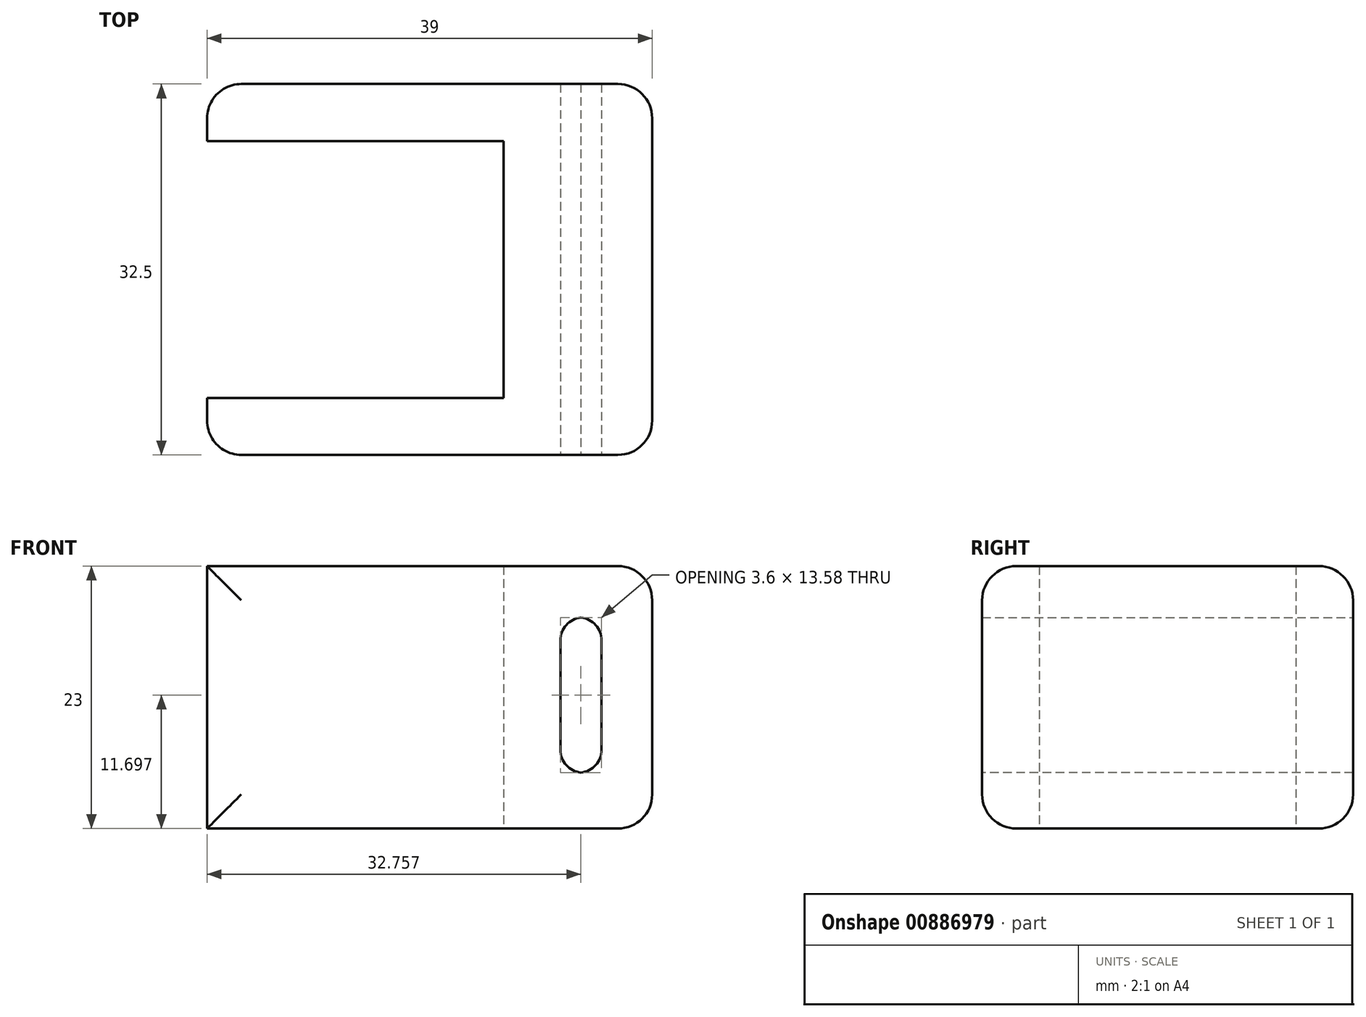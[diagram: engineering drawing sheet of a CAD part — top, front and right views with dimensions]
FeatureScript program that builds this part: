
annotation { "Feature Type Name" : "Feature", "Feature Type Description" : "" }
export const myFeature = defineFeature(function(context is Context, id is Id, definition is map)
    precondition{}
    {
        {
            var Q0;
            Q0=qCreatedBy(makeId("Top.planeOp"),FACE);
            var sketch = newSketch(context, id + "F0", { "sketchPlane" : qUnion([Q0])});
            skLineSegment(sketch, "E0", {"start": v(12.77, 15.26) * mm, "end": v(12.77, -17.24) * mm});
            skLineSegment(sketch, "E1", {"start": v(12.77, -17.24) * mm, "end": v(-26.23, -17.24) * mm});
            skLineSegment(sketch, "E2", {"start": v(-26.23, -17.24) * mm, "end": v(-26.23, -12.24) * mm});
            skLineSegment(sketch, "E3", {"start": v(-26.23, -12.24) * mm, "end": v(-0.23, -12.24) * mm});
            skLineSegment(sketch, "E4", {"start": v(-0.23, -12.24) * mm, "end": v(-0.23, 10.26) * mm});
            skLineSegment(sketch, "E5", {"start": v(-0.23, 10.26) * mm, "end": v(-26.23, 10.26) * mm});
            skLineSegment(sketch, "E6", {"start": v(-26.23, 10.26) * mm, "end": v(-26.23, 15.26) * mm});
            skLineSegment(sketch, "E7", {"start": v(-26.23, 15.26) * mm, "end": v(12.77, 15.26) * mm});
            skSolve(sketch);
        }
        {
            var Q0;
            Q0=makeQuery(id+"F0.imprint","IMPRINT",FACE,{"disambiguationData":[TD([[makeQuery(id+"F0.imprint","IMPRINT",EDGE,{"derivedFrom":sQuery(id+"F0.wireOp",EDGE,"E0")}),-1.0]])]});
            extrude(context, id + "F1", {"entities" : qUnion([Q0]), "depth" : 23 * mm, "offsetDistance" : 25 * mm});
        }
        {
            var Q0;
            Q0=makeQuery(id+"F1.opExtrude","SWEPT_FACE",FACE,{"disambiguationData":[OSD([sQuery(id+"F0.wireOp",EDGE,"E1")])]});
            var sketch = newSketch(context, id + "F2", { "sketchPlane" : qUnion([Q0])});
            skLineSegment(sketch, "E8.bottom", {"start": v(8.33, 18.5) * mm, "end": v(4.73, 18.5) * mm});
            skLineSegment(sketch, "E8.top", {"start": v(8.33, 4.9) * mm, "end": v(4.73, 4.9) * mm});
            skLineSegment(sketch, "E8.left", {"start": v(8.33, 18.5) * mm, "end": v(8.33, 4.9) * mm});
            skLineSegment(sketch, "E8.right", {"start": v(4.73, 18.5) * mm, "end": v(4.73, 4.9) * mm});
            skSolve(sketch);
        }
        {
            var Q0;
            Q0=makeQuery(id+"F2.imprint","IMPRINT",FACE,{"disambiguationData":[TD([[makeQuery(id+"F2.imprint","IMPRINT",EDGE,{"derivedFrom":sQuery(id+"F2.wireOp",EDGE,"E8.bottom")}),1.0]])]});
            extrude(context, id + "F3", {"entities" : qUnion([Q0]), "operationType" : NewBodyOperationType.REMOVE, "oppositeDirection" : true, "depth" : 48.7 * mm, "offsetDistance" : 25 * mm});
        }
        {
            var Q0;
            Q0=makeQuery(id+"F3.boolean.opBoolean","COPY",EDGE,{"derivedFrom":makeQuery(id+"F3.opExtrude","SWEPT_EDGE",EDGE,{"disambiguationData":[OSD([sQuery(id+"F2.wireOp",EDGE,"E8.bottom"),sQuery(id+"F2.wireOp",EDGE,"E8.right")])]})});
            var Q1;
            Q1=makeQuery(id+"F3.boolean.opBoolean","COPY",EDGE,{"derivedFrom":makeQuery(id+"F3.opExtrude","SWEPT_EDGE",EDGE,{"disambiguationData":[OSD([sQuery(id+"F2.wireOp",EDGE,"E8.top"),sQuery(id+"F2.wireOp",EDGE,"E8.right")])]})});
            var Q2;
            Q2=makeQuery(id+"F3.boolean.opBoolean","COPY",EDGE,{"derivedFrom":makeQuery(id+"F3.opExtrude","SWEPT_EDGE",EDGE,{"disambiguationData":[OSD([sQuery(id+"F2.wireOp",EDGE,"E8.bottom"),sQuery(id+"F2.wireOp",EDGE,"E8.left")])]})});
            var Q3;
            Q3=makeQuery(id+"F3.boolean.opBoolean","COPY",EDGE,{"derivedFrom":makeQuery(id+"F3.opExtrude","SWEPT_EDGE",EDGE,{"disambiguationData":[OSD([sQuery(id+"F2.wireOp",EDGE,"E8.top"),sQuery(id+"F2.wireOp",EDGE,"E8.left")])]})});
            fillet(context, id + "F4", {"entities" : qUnion([Q0, Q1, Q2, Q3]), "radius" : 2 * mm, "tangentPropagation" : true, "allowEdgeOverflow" : false});
        }
        {
            var Q0;
            Q0=makeQuery(id+"F1.opExtrude","CAP_EDGE",EDGE,{"disambiguationData":[OSD([sQuery(id+"F0.wireOp",EDGE,"E7")])],"isStart":true});
            var Q1;
            Q1=makeQuery(id+"F1.opExtrude","SWEPT_EDGE",EDGE,{"disambiguationData":[OSD([sQuery(id+"F0.wireOp",EDGE,"E6"),sQuery(id+"F0.wireOp",EDGE,"E7")])]});
            var Q2;
            Q2=makeQuery(id+"F1.opExtrude","CAP_EDGE",EDGE,{"disambiguationData":[OSD([sQuery(id+"F0.wireOp",EDGE,"E7")])],"isStart":false});
            var Q3;
            Q3=makeQuery(id+"F1.opExtrude","CAP_EDGE",EDGE,{"disambiguationData":[OSD([sQuery(id+"F0.wireOp",EDGE,"E1")])],"isStart":false});
            var Q4;
            Q4=makeQuery(id+"F1.opExtrude","CAP_EDGE",EDGE,{"disambiguationData":[OSD([sQuery(id+"F0.wireOp",EDGE,"E0")])],"isStart":false});
            var Q5;
            Q5=makeQuery(id+"F1.opExtrude","CAP_EDGE",EDGE,{"disambiguationData":[OSD([sQuery(id+"F0.wireOp",EDGE,"E1")])],"isStart":true});
            var Q6;
            Q6=makeQuery(id+"F1.opExtrude","CAP_EDGE",EDGE,{"disambiguationData":[OSD([sQuery(id+"F0.wireOp",EDGE,"E0")])],"isStart":true});
            var Q7;
            Q7=makeQuery(id+"F1.opExtrude","SWEPT_EDGE",EDGE,{"disambiguationData":[OSD([sQuery(id+"F0.wireOp",EDGE,"E0"),sQuery(id+"F0.wireOp",EDGE,"E1")])]});
            var Q8;
            Q8=makeQuery(id+"F1.opExtrude","SWEPT_EDGE",EDGE,{"disambiguationData":[OSD([sQuery(id+"F0.wireOp",EDGE,"E0"),sQuery(id+"F0.wireOp",EDGE,"E7")])]});
            var Q9;
            Q9=makeQuery(id+"F1.opExtrude","SWEPT_EDGE",EDGE,{"disambiguationData":[OSD([sQuery(id+"F0.wireOp",EDGE,"E1"),sQuery(id+"F0.wireOp",EDGE,"E2")])]});
            fillet(context, id + "F5", {"entities" : qUnion([Q0, Q1, Q2, Q3, Q4, Q5, Q6, Q7, Q8, Q9]), "radius" : 3 * mm, "tangentPropagation" : true, "allowEdgeOverflow" : false});
        }
    });
